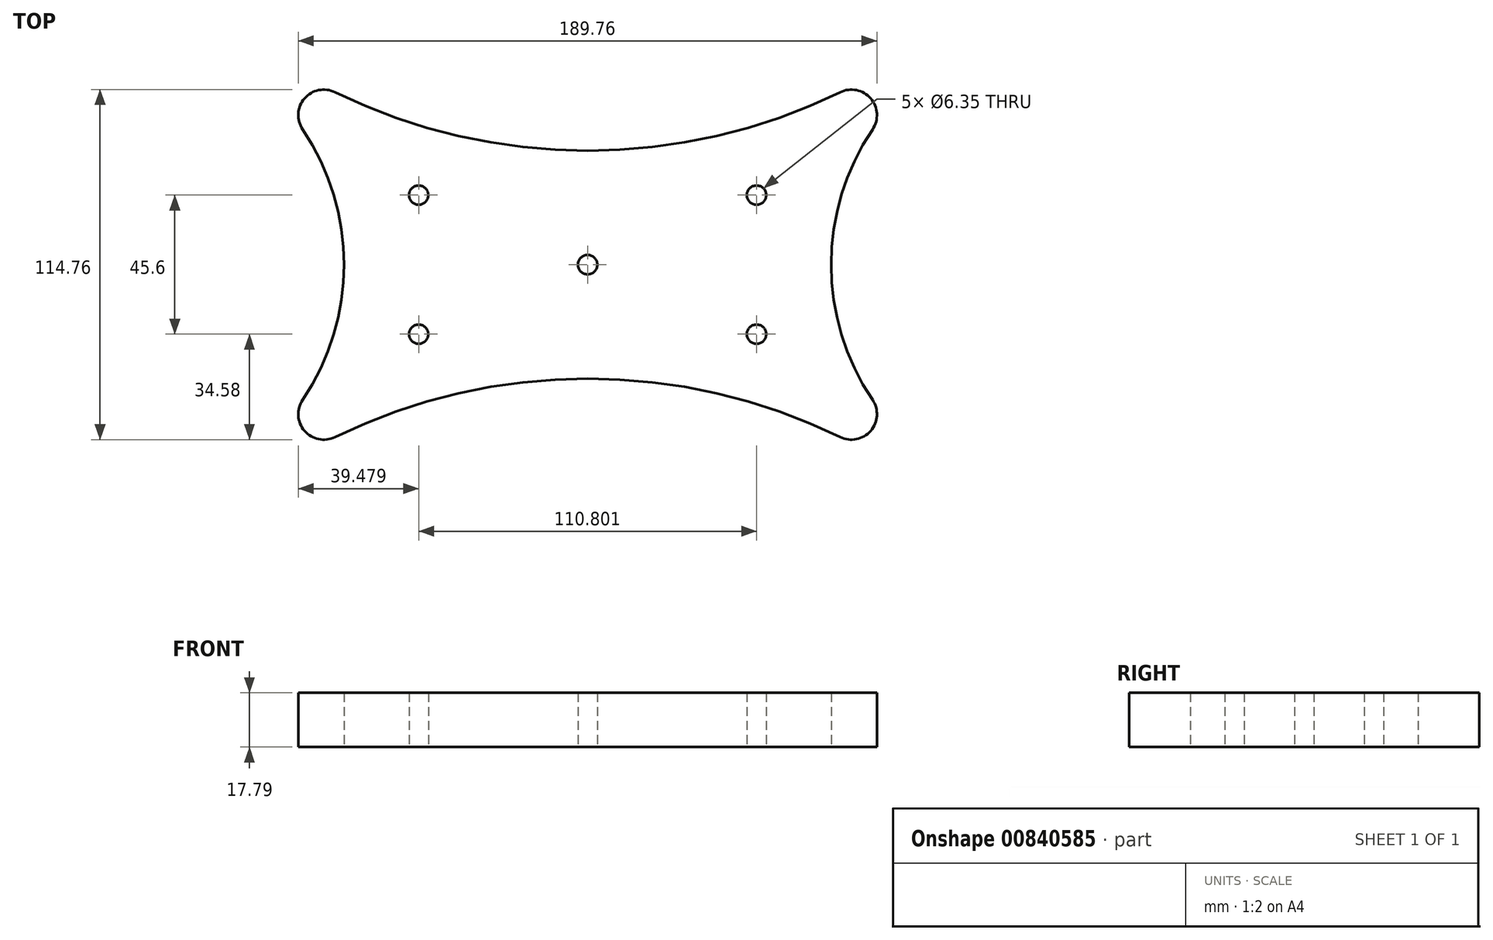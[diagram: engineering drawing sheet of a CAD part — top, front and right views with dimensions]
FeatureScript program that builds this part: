
annotation { "Feature Type Name" : "Feature", "Feature Type Description" : "" }
export const myFeature = defineFeature(function(context is Context, id is Id, definition is map)
    precondition{}
    {
        {
            var Q0;
            Q0=qCreatedBy(makeId("Top.planeOp"),FACE);
            var sketch = newSketch(context, id + "F0", { "sketchPlane" : qUnion([Q0])});
            skLineSegment(sketch, "E0.bottom", {"start": v(-102.5, 65) * mm, "end": v(102.5, 65) * mm, "construction": true});
            skLineSegment(sketch, "E0.top", {"start": v(-102.5, -65) * mm, "end": v(102.5, -65) * mm, "construction": true});
            skLineSegment(sketch, "E0.left", {"start": v(-102.5, 65) * mm, "end": v(-102.5, -65) * mm, "construction": true});
            skLineSegment(sketch, "E0.right", {"start": v(102.5, 65) * mm, "end": v(102.5, -65) * mm, "construction": true});
            skPoint(sketch, "E0.middle", {"position": v(0, 0) * mm});
            skArc(sketch, "E1", {"start": v(-79.48, 63.38) * mm, "mid": v(-98.58, 59.5) * mm, "end": v(-99.76, 40.04) * mm, "construction": true});
            skArc(sketch, "E2.MirrorC", {"start": v(79.48, 63.38) * mm, "mid": v(98.58, 59.5) * mm, "end": v(99.76, 40.04) * mm, "construction": true});
            skArc(sketch, "E3.MirrorC", {"start": v(79.48, -63.38) * mm, "mid": v(98.58, -59.5) * mm, "end": v(99.76, -40.04) * mm, "construction": true});
            skArc(sketch, "E4.MirrorC", {"start": v(-79.48, -63.38) * mm, "mid": v(-98.58, -59.5) * mm, "end": v(-99.76, -40.04) * mm, "construction": true});
            skLineSegment(sketch, "E5", {"start": v(0, 0) * mm, "end": v(0, 365.73) * mm, "construction": true});
            skPoint(sketch, "E5.endSnap0", {"position": v(0, 65) * mm});
            skLineSegment(sketch, "E6", {"start": v(0, 0) * mm, "end": v(0, -420.15) * mm, "construction": true});
            skLineSegment(sketch, "E7", {"start": v(0, 0) * mm, "end": v(397.25, 0) * mm, "construction": true});
            skPoint(sketch, "E7.endSnap0", {"position": v(102.5, 0) * mm});
            skLineSegment(sketch, "E8", {"start": v(0, 0) * mm, "end": v(-430.2, 0) * mm, "construction": true});
            skPoint(sketch, "E9", {"position": v(0, 45) * mm});
            skPoint(sketch, "E10", {"position": v(0, -45) * mm});
            skPoint(sketch, "E11", {"position": v(-87.5, 0) * mm});
            skPoint(sketch, "E12", {"position": v(87.5, 0) * mm});
            skArc(sketch, "E13", {"start": v(-79.48, 63.38) * mm, "mid": v(0, 45) * mm, "end": v(79.48, 63.38) * mm, "construction": true});
            skArc(sketch, "E14.MirrorC", {"start": v(-79.48, -63.38) * mm, "mid": v(0, -45) * mm, "end": v(79.48, -63.38) * mm, "construction": true});
            skArc(sketch, "E15", {"start": v(99.76, 40.04) * mm, "mid": v(87.5, 0) * mm, "end": v(99.76, -40.04) * mm, "construction": true});
            skArc(sketch, "E16.MirrorC", {"start": v(-99.76, 40.04) * mm, "mid": v(-87.5, 0) * mm, "end": v(-99.76, -40.04) * mm, "construction": true});
            skArc(sketch, "E17", {"start": v(-12.5, 12.5) * mm, "mid": v(-25, 0) * mm, "end": v(-12.5, -12.5) * mm, "construction": true});
            skArc(sketch, "E18.MirrorC", {"start": v(12.5, 12.5) * mm, "mid": v(25, 0) * mm, "end": v(12.5, -12.5) * mm, "construction": true});
            skLineSegment(sketch, "E19", {"start": v(-12.5, 12.5) * mm, "end": v(12.5, 12.5) * mm, "construction": true});
            skLineSegment(sketch, "E20", {"start": v(-12.5, -12.5) * mm, "end": v(12.5, -12.5) * mm, "construction": true});
            skArc(sketch, "E21.0", {"start": v(-82.82, 56.53) * mm, "mid": v(-92.82, 54.5) * mm, "end": v(-93.44, 44.3) * mm});
            skArc(sketch, "E21.1", {"start": v(-93.44, 44.3) * mm, "mid": v(-79.88, 0) * mm, "end": v(-93.44, -44.3) * mm});
            skArc(sketch, "E21.2", {"start": v(-82.82, 56.53) * mm, "mid": v(0, 37.38) * mm, "end": v(82.82, 56.53) * mm});
            skArc(sketch, "E21.3", {"start": v(-82.82, -56.53) * mm, "mid": v(-92.82, -54.5) * mm, "end": v(-93.44, -44.3) * mm});
            skArc(sketch, "E21.4", {"start": v(82.82, 56.53) * mm, "mid": v(92.82, 54.5) * mm, "end": v(93.44, 44.3) * mm});
            skArc(sketch, "E21.5", {"start": v(93.44, 44.3) * mm, "mid": v(79.88, 0) * mm, "end": v(93.44, -44.3) * mm});
            skArc(sketch, "E21.6", {"start": v(82.82, -56.53) * mm, "mid": v(92.82, -54.5) * mm, "end": v(93.44, -44.3) * mm});
            skArc(sketch, "E21.7", {"start": v(-82.82, -56.53) * mm, "mid": v(0, -37.38) * mm, "end": v(82.82, -56.53) * mm});
            skLineSegment(sketch, "E22.0", {"start": v(-12.5, 20.12) * mm, "end": v(12.5, 20.12) * mm, "construction": true});
            skArc(sketch, "E22.1", {"start": v(-12.5, 20.12) * mm, "mid": v(-32.62, 0) * mm, "end": v(-12.5, -20.12) * mm, "construction": true});
            skLineSegment(sketch, "E22.2", {"start": v(-12.5, -20.12) * mm, "end": v(12.5, -20.12) * mm, "construction": true});
            skArc(sketch, "E22.3", {"start": v(12.5, 20.12) * mm, "mid": v(32.62, 0) * mm, "end": v(12.5, -20.12) * mm, "construction": true});
            skPoint(sketch, "E23", {"position": v(-55.4, 22.8) * mm});
            skPoint(sketch, "E24.MirrorP", {"position": v(55.4, 22.8) * mm});
            skCircle(sketch, "E25", {"center": v(-55.4, -22.8) * mm, "radius": 3.18 * mm});
            skCircle(sketch, "E26.MirrorC", {"center": v(-55.4, 22.8) * mm, "radius": 3.18 * mm});
            skCircle(sketch, "E27.MirrorC", {"center": v(55.4, 22.8) * mm, "radius": 3.18 * mm});
            skCircle(sketch, "E28.MirrorC", {"center": v(55.4, -22.8) * mm, "radius": 3.18 * mm});
            skCircle(sketch, "E29", {"center": v(0, 0) * mm, "radius": 3.18 * mm});
            skSolve(sketch);
        }
        {
            var Q0;
            Q0=makeQuery(id+"F0.imprint","IMPRINT",FACE,{"disambiguationData":[TD([[makeQuery(id+"F0.imprint","IMPRINT",EDGE,{"derivedFrom":sQuery(id+"F0.wireOp",EDGE,"E21.0")}),1.0]])]});
            extrude(context, id + "F1", {"entities" : qUnion([Q0]), "depth" : 19.05 * mm, "offsetDistance" : 25.4 * mm});
        }
        {
            var Q0;
            Q0=makeQuery(id+"F0.imprint","IMPRINT",FACE,{"disambiguationData":[TD([[makeQuery(id+"F0.imprint","IMPRINT",EDGE,{"derivedFrom":sQuery(id+"F0.wireOp",EDGE,"7149383d-6806-47e7-955f-45070dd5f411.0")}),1.0]])]});
            var Q1;
            Q1=makeQuery(id+"F0.imprint","IMPRINT",FACE,{"disambiguationData":[TD([[makeQuery(id+"F0.imprint","IMPRINT",EDGE,{"derivedFrom":sQuery(id+"F0.wireOp",EDGE,"4d6d176b-095b-43fb-b494-88346d599ebd.0")}),1.0]])]});
            var Q2;
            Q2=makeQuery(id+"F0.imprint","IMPRINT",FACE,{"disambiguationData":[TD([[makeQuery(id+"F0.imprint","IMPRINT",EDGE,{"derivedFrom":sQuery(id+"F0.wireOp",EDGE,"4b4786f8-b92a-4d9f-973b-bd4f317ae80a.0")}),1.0]])]});
            var Q3;
            Q3=makeQuery(id+"F0.imprint","IMPRINT",FACE,{"disambiguationData":[TD([[makeQuery(id+"F0.imprint","IMPRINT",EDGE,{"derivedFrom":sQuery(id+"F0.wireOp",EDGE,"0d8905ca-489c-47ad-a59a-d1c3a2a1c8b4.0")}),1.0]])]});
            var Q4;
            Q4=makeQuery(id+"F0.imprint","IMPRINT",FACE,{"disambiguationData":[TD([[makeQuery(id+"F0.imprint","IMPRINT",EDGE,{"derivedFrom":sQuery(id+"F0.wireOp",EDGE,"5e8b5514-13b3-4359-a275-61de55d9f6221.MirrorCS")}),-1.0]])]});
            var Q5;
            Q5=makeQuery(id+"F0.imprint","IMPRINT",FACE,{"disambiguationData":[TD([[makeQuery(id+"F0.imprint","IMPRINT",EDGE,{"derivedFrom":sQuery(id+"F0.wireOp",EDGE,"5e8b5514-13b3-4359-a275-61de55d9f62211.MirrorCS")}),1.0]])]});
            var Q6;
            Q6=makeQuery(id+"F0.imprint","IMPRINT",FACE,{"disambiguationData":[TD([[makeQuery(id+"F0.imprint","IMPRINT",EDGE,{"derivedFrom":sQuery(id+"F0.wireOp",EDGE,"E25")}),-1.0]])]});
            var Q7;
            Q7=makeQuery(id+"F0.imprint","IMPRINT",FACE,{"disambiguationData":[TD([[makeQuery(id+"F0.imprint","IMPRINT",EDGE,{"derivedFrom":sQuery(id+"F0.wireOp",EDGE,"5a64c7df-c07c-4376-a7bf-d3305ba3e5c70.MirrorCS")}),1.0]])]});
            extrude(context, id + "F2", {"entities" : qUnion([Q0, Q1, Q2, Q3, Q4, Q5, Q6, Q7]), "operationType" : NewBodyOperationType.ADD, "depth" : 22.22 * mm, "offsetDistance" : 25.4 * mm});
        }
        {
            var Q0;
            Q0=makeQuery(id+"F0.imprint","IMPRINT",FACE,{"disambiguationData":[TD([[makeQuery(id+"F0.imprint","IMPRINT",EDGE,{"derivedFrom":sQuery(id+"F0.wireOp",EDGE,"5a64c7df-c07c-4376-a7bf-d3305ba3e5c70.MirrorCS")}),1.0]])]});
            var Q1;
            Q1=makeQuery(id+"F0.imprint","IMPRINT",FACE,{"disambiguationData":[TD([[makeQuery(id+"F0.imprint","IMPRINT",EDGE,{"derivedFrom":sQuery(id+"F0.wireOp",EDGE,"5e8b5514-13b3-4359-a275-61de55d9f6221.MirrorCS")}),-1.0]])]});
            var Q2;
            Q2=makeQuery(id+"F0.imprint","IMPRINT",FACE,{"disambiguationData":[TD([[makeQuery(id+"F0.imprint","IMPRINT",EDGE,{"derivedFrom":sQuery(id+"F0.wireOp",EDGE,"5e8b5514-13b3-4359-a275-61de55d9f62211.MirrorCS")}),1.0]])]});
            var Q3;
            Q3=makeQuery(id+"F0.imprint","IMPRINT",FACE,{"disambiguationData":[TD([[makeQuery(id+"F0.imprint","IMPRINT",EDGE,{"derivedFrom":sQuery(id+"F0.wireOp",EDGE,"E25")}),-1.0]])]});
            extrude(context, id + "F3", {"entities" : qUnion([Q0, Q1, Q2, Q3]), "operationType" : NewBodyOperationType.REMOVE, "depth" : 4.44 * mm, "offsetDistance" : 25.4 * mm});
        }
    });
